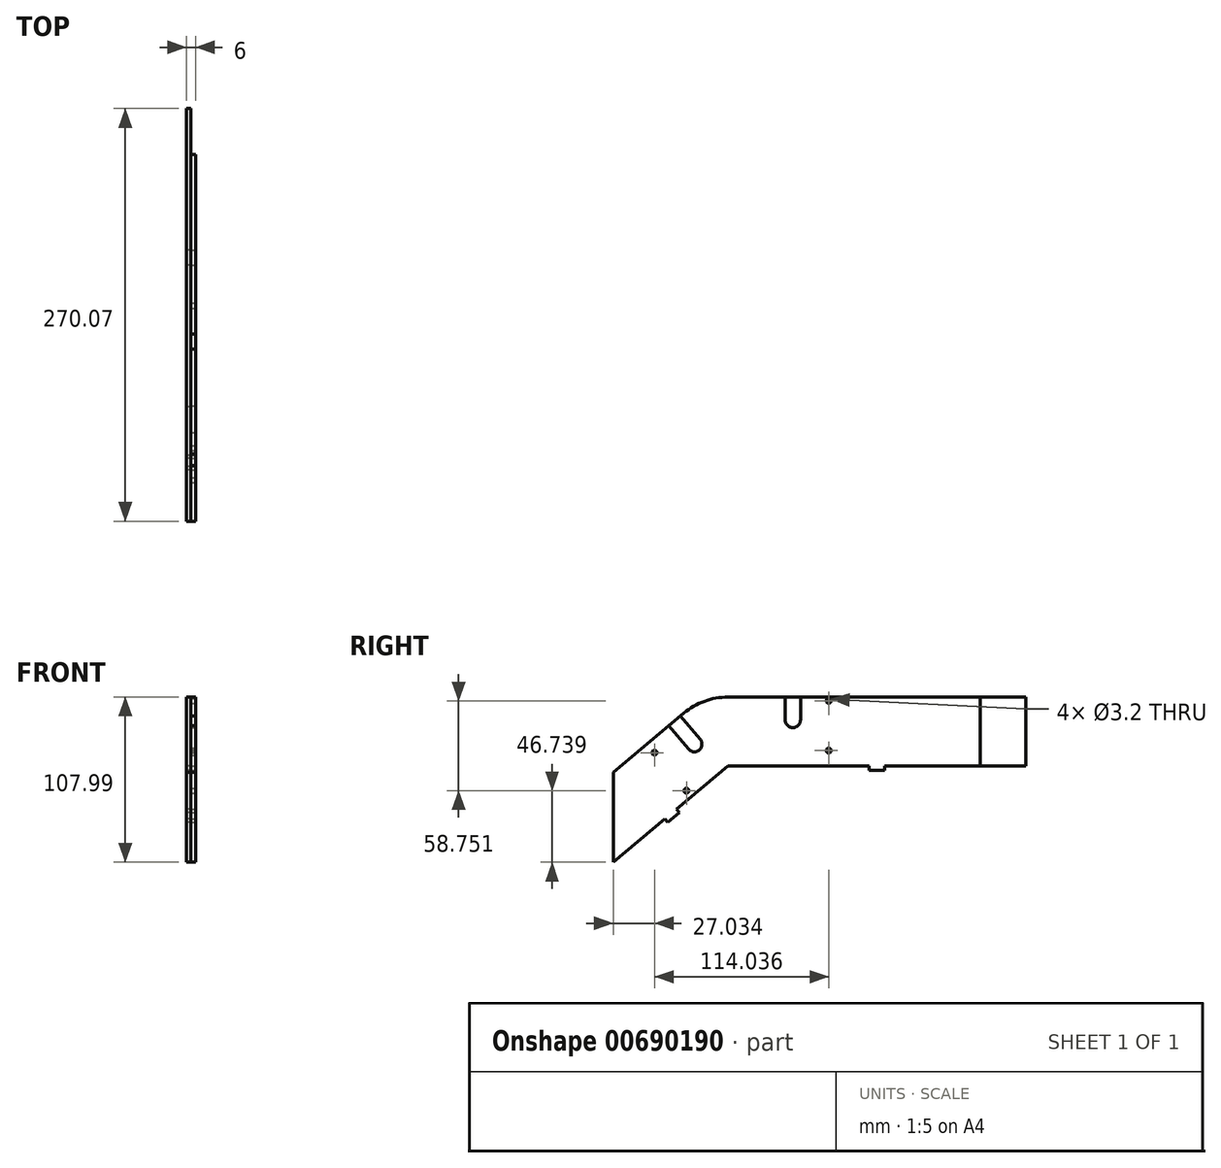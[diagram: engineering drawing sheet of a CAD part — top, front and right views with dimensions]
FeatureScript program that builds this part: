
annotation { "Feature Type Name" : "Feature", "Feature Type Description" : "" }
export const myFeature = defineFeature(function(context is Context, id is Id, definition is map)
    precondition{}
    {
        {
            var Q0;
            Q0=qCreatedBy(makeId("Right.planeOp"),FACE);
            var sketch = newSketch(context, id + "F0", { "sketchPlane" : qUnion([Q0])});
            skLineSegment(sketch, "E0.bottom", {"start": v(-97.5, 0) * mm, "end": v(97.5, 0) * mm});
            skLineSegment(sketch, "E0.top", {"start": v(-97.5, 45) * mm, "end": v(97.5, 45) * mm});
            skLineSegment(sketch, "E0.left", {"start": v(-97.5, 0) * mm, "end": v(-97.5, 45) * mm, "construction": true});
            skLineSegment(sketch, "E0.right", {"start": v(97.5, 0) * mm, "end": v(97.5, 45) * mm});
            skPoint(sketch, "E0.middle", {"position": v(0, 22.5) * mm});
            skLineSegment(sketch, "E1", {"start": v(-97.5, 0) * mm, "end": v(-172.57, -63) * mm});
            skLineSegment(sketch, "E2", {"start": v(-172.57, -63) * mm, "end": v(-201.5, -28.52) * mm});
            skLineSegment(sketch, "E3", {"start": v(-201.5, -28.52) * mm, "end": v(-126.43, 34.47) * mm});
            skLineSegment(sketch, "E4", {"start": v(-97.5, 0) * mm, "end": v(-126.43, 34.47) * mm, "construction": true});
            skArc(sketch, "E5", {"start": v(-97.5, 45) * mm, "mid": v(-112.9, 42.29) * mm, "end": v(-126.43, 34.47) * mm});
            skSolve(sketch);
        }
        {
            var Q0;
            Q0=makeQuery(id+"F0.imprint","IMPRINT",FACE,{"disambiguationData":[TD([[makeQuery(id+"F0.imprint","IMPRINT",EDGE,{"derivedFrom":sQuery(id+"F0.wireOp",EDGE,"E0.bottom")}),1.0]])]});
            extrude(context, id + "F1", {"entities" : qUnion([Q0]), "depth" : 3 * mm, "offsetDistance" : 25 * mm});
        }
        {
            var Q0;
            Q0=makeQuery(id+"F1.opExtrude","CAP_FACE",FACE,{"disambiguationData":[OSD([sQuery(id+"F0.wireOp",EDGE,"E0.bottom"),sQuery(id+"F0.wireOp",EDGE,"E0.top"),sQuery(id+"F0.wireOp",EDGE,"E0.left"),sQuery(id+"F0.wireOp",EDGE,"E0.right")])],"isStart":false});
            var sketch = newSketch(context, id + "F2", { "sketchPlane" : qUnion([Q0])});
            skLineSegment(sketch, "E6.bottom", {"start": v(4.95, 0) * mm, "end": v(-4.95, 0) * mm});
            skLineSegment(sketch, "E6.top", {"start": v(4.95, -3) * mm, "end": v(-4.95, -3) * mm});
            skLineSegment(sketch, "E6.left", {"start": v(4.95, 0) * mm, "end": v(4.95, -3) * mm});
            skLineSegment(sketch, "E6.right", {"start": v(-4.95, 0) * mm, "end": v(-4.95, -3) * mm});
            skPoint(sketch, "E6.middle", {"position": v(0, -1.5) * mm});
            skLineSegment(sketch, "E7", {"start": v(-138.83, -34.68) * mm, "end": v(-136.9, -36.98) * mm});
            skLineSegment(sketch, "E8", {"start": v(-136.9, -36.98) * mm, "end": v(-129.32, -30.61) * mm});
            skLineSegment(sketch, "E9", {"start": v(-129.32, -30.61) * mm, "end": v(-131.24, -28.31) * mm});
            skLineSegment(sketch, "E10", {"start": v(-131.24, -28.31) * mm, "end": v(-138.83, -34.68) * mm});
            skSolve(sketch);
        }
        {
            var Q0;
            Q0=makeQuery(id+"F2.imprint","IMPRINT",FACE,{"disambiguationData":[TD([[makeQuery(id+"F2.imprint","IMPRINT",EDGE,{"derivedFrom":sQuery(id+"F2.wireOp",EDGE,"E6.bottom")}),-1.0]])]});
            var Q1;
            Q1=makeQuery(id+"F2.imprint","IMPRINT",FACE,{"disambiguationData":[TD([[makeQuery(id+"F2.imprint","IMPRINT",EDGE,{"derivedFrom":sQuery(id+"F2.wireOp",EDGE,"E7")}),1.0]])]});
            var Q2;
            Q2=makeQuery(id+"F1.opExtrude","CAP_FACE",FACE,{"disambiguationData":[OSD([sQuery(id+"F0.wireOp",EDGE,"E0.bottom"),sQuery(id+"F0.wireOp",EDGE,"E0.top"),sQuery(id+"F0.wireOp",EDGE,"E0.left"),sQuery(id+"F0.wireOp",EDGE,"E0.right")])],"isStart":true});
            extrude(context, id + "F3", {"entities" : qUnion([Q0, Q1]), "operationType" : NewBodyOperationType.ADD, "endBound" : BoundingType.UP_TO_SURFACE, "oppositeDirection" : true, "depth" : 25 * mm, "endBoundEntityFace" : qUnion([Q2]), "offsetDistance" : 25 * mm});
        }
        {
            var Q0;
            Q0=makeQuery(id+"F3.boolean.opBoolean","MERGE",FACE,{"derivedFrom":[makeQuery(id+"F1.opExtrude","CAP_FACE",FACE,{"disambiguationData":[OSD([sQuery(id+"F0.wireOp",EDGE,"E0.bottom"),sQuery(id+"F0.wireOp",EDGE,"E0.top"),sQuery(id+"F0.wireOp",EDGE,"E0.right"),sQuery(id+"F0.wireOp",EDGE,"E1"),sQuery(id+"F0.wireOp",EDGE,"E2"),sQuery(id+"F0.wireOp",EDGE,"E3"),sQuery(id+"F0.wireOp",EDGE,"E5")])],"isStart":false}),makeQuery(id+"F3.opExtrude","CAP_FACE",FACE,{"disambiguationData":[OSD([sQuery(id+"F2.wireOp",EDGE,"E6.bottom"),sQuery(id+"F2.wireOp",EDGE,"E6.top"),sQuery(id+"F2.wireOp",EDGE,"E6.left"),sQuery(id+"F2.wireOp",EDGE,"E6.right")])],"isStart":true}),makeQuery(id+"F3.opExtrude","CAP_FACE",FACE,{"disambiguationData":[OSD([sQuery(id+"F2.wireOp",EDGE,"E7"),sQuery(id+"F2.wireOp",EDGE,"E8"),sQuery(id+"F2.wireOp",EDGE,"E9"),sQuery(id+"F2.wireOp",EDGE,"E10")])],"isStart":true})]});
            var sketch = newSketch(context, id + "F4", { "sketchPlane" : qUnion([Q0])});
            skLineSegment(sketch, "E11", {"start": v(-172.57, -63) * mm, "end": v(-172.57, -4.25) * mm});
            skLineSegment(sketch, "E12", {"start": v(-172.57, -4.25) * mm, "end": v(-201.5, -28.52) * mm});
            skLineSegment(sketch, "E13", {"start": v(-201.5, -28.52) * mm, "end": v(-172.57, -63) * mm});
            skSolve(sketch);
        }
        {
            var Q0;
            Q0=makeQuery(id+"F4.imprint","IMPRINT",FACE,{"disambiguationData":[TD([[makeQuery(id+"F4.imprint","IMPRINT",EDGE,{"derivedFrom":sQuery(id+"F4.wireOp",EDGE,"E11")}),1.0]])]});
            extrude(context, id + "F5", {"entities" : qUnion([Q0]), "operationType" : NewBodyOperationType.REMOVE, "endBound" : BoundingType.UP_TO_NEXT, "oppositeDirection" : true, "depth" : 25 * mm, "offsetDistance" : 25 * mm});
        }
        {
            var Q0;
            Q0=makeQuery(id+"F1.opExtrude","SWEPT_BODY",BODY,{"disambiguationData":[OSD([sQuery(id+"F0.wireOp",EDGE,"E0.bottom"),sQuery(id+"F0.wireOp",EDGE,"E0.top"),sQuery(id+"F0.wireOp",EDGE,"E0.left"),sQuery(id+"F0.wireOp",EDGE,"E0.right")])]});
            var Q1;
            Q1=qCreatedBy(makeId("Right.planeOp"),FACE);
            mirror(context, id + "F6", {"entities" : qUnion([Q0]), "mirrorPlane" : qUnion([Q1])});
        }
        {
            var Q0;
            Q0=makeQuery(id+"F3.boolean.opBoolean","MERGE",FACE,{"derivedFrom":[makeQuery(id+"F1.opExtrude","CAP_FACE",FACE,{"disambiguationData":[OSD([sQuery(id+"F0.wireOp",EDGE,"E0.bottom"),sQuery(id+"F0.wireOp",EDGE,"E0.top"),sQuery(id+"F0.wireOp",EDGE,"E0.right"),sQuery(id+"F0.wireOp",EDGE,"E1"),sQuery(id+"F0.wireOp",EDGE,"E2"),sQuery(id+"F0.wireOp",EDGE,"E3"),sQuery(id+"F0.wireOp",EDGE,"E5")])],"isStart":false}),makeQuery(id+"F3.opExtrude","CAP_FACE",FACE,{"disambiguationData":[OSD([sQuery(id+"F2.wireOp",EDGE,"E6.bottom"),sQuery(id+"F2.wireOp",EDGE,"E6.top"),sQuery(id+"F2.wireOp",EDGE,"E6.left"),sQuery(id+"F2.wireOp",EDGE,"E6.right")])],"isStart":true}),makeQuery(id+"F3.opExtrude","CAP_FACE",FACE,{"disambiguationData":[OSD([sQuery(id+"F2.wireOp",EDGE,"E7"),sQuery(id+"F2.wireOp",EDGE,"E8"),sQuery(id+"F2.wireOp",EDGE,"E9"),sQuery(id+"F2.wireOp",EDGE,"E10")])],"isStart":true})]});
            var sketch = newSketch(context, id + "F7", { "sketchPlane" : qUnion([Q0])});
            skLineSegment(sketch, "E14.bottom", {"start": v(97.5, 45) * mm, "end": v(67.5, 45) * mm});
            skLineSegment(sketch, "E14.top", {"start": v(97.5, 0) * mm, "end": v(67.5, 0) * mm});
            skLineSegment(sketch, "E14.left", {"start": v(97.5, 45) * mm, "end": v(97.5, 0) * mm});
            skLineSegment(sketch, "E14.right", {"start": v(67.5, 45) * mm, "end": v(67.5, 0) * mm});
            skSolve(sketch);
        }
        {
            var Q0;
            Q0=makeQuery(id+"F7.imprint","IMPRINT",FACE,{"disambiguationData":[TD([[makeQuery(id+"F7.imprint","IMPRINT",EDGE,{"derivedFrom":sQuery(id+"F7.wireOp",EDGE,"E14.bottom")}),-1.0]])]});
            extrude(context, id + "F8", {"entities" : qUnion([Q0]), "operationType" : NewBodyOperationType.REMOVE, "endBound" : BoundingType.UP_TO_NEXT, "oppositeDirection" : true, "depth" : 25 * mm, "offsetDistance" : 25 * mm});
        }
        {
            var Q0;
            Q0=makeQuery(id+"F3.boolean.opBoolean","MERGE",FACE,{"derivedFrom":[makeQuery(id+"F1.opExtrude","CAP_FACE",FACE,{"disambiguationData":[OSD([sQuery(id+"F0.wireOp",EDGE,"E0.bottom"),sQuery(id+"F0.wireOp",EDGE,"E0.top"),sQuery(id+"F0.wireOp",EDGE,"E0.right"),sQuery(id+"F0.wireOp",EDGE,"E1"),sQuery(id+"F0.wireOp",EDGE,"E2"),sQuery(id+"F0.wireOp",EDGE,"E3"),sQuery(id+"F0.wireOp",EDGE,"E5")])],"isStart":false}),makeQuery(id+"F3.opExtrude","CAP_FACE",FACE,{"disambiguationData":[OSD([sQuery(id+"F2.wireOp",EDGE,"E6.bottom"),sQuery(id+"F2.wireOp",EDGE,"E6.top"),sQuery(id+"F2.wireOp",EDGE,"E6.left"),sQuery(id+"F2.wireOp",EDGE,"E6.right")])],"isStart":true}),makeQuery(id+"F3.opExtrude","CAP_FACE",FACE,{"disambiguationData":[OSD([sQuery(id+"F2.wireOp",EDGE,"E7"),sQuery(id+"F2.wireOp",EDGE,"E8"),sQuery(id+"F2.wireOp",EDGE,"E9"),sQuery(id+"F2.wireOp",EDGE,"E10")])],"isStart":true})]});
            var sketch = newSketch(context, id + "F9", { "sketchPlane" : qUnion([Q0])});
            skLineSegment(sketch, "E15", {"start": v(-145.54, 8.65) * mm, "end": v(-124.65, -16.25) * mm, "construction": true});
            skSolve(sketch);
        }
        {
            var Q0;
            Q0=sQuery(id+"F9.wireOp",VERTEX,"E15.end");
            var Q1;
            Q1=sQuery(id+"F9.wireOp",VERTEX,"E15.start");
            var Q2;
            Q2=makeQuery(id+"F1.opExtrude","SWEPT_BODY",BODY,{"disambiguationData":[OSD([sQuery(id+"F0.wireOp",EDGE,"E0.bottom"),sQuery(id+"F0.wireOp",EDGE,"E0.top"),sQuery(id+"F0.wireOp",EDGE,"E0.right"),sQuery(id+"F0.wireOp",EDGE,"E1"),sQuery(id+"F0.wireOp",EDGE,"E2"),sQuery(id+"F0.wireOp",EDGE,"E3"),sQuery(id+"F0.wireOp",EDGE,"E5")])]});
            hole(context, id + "F10", {"style" : HoleStyle.SIMPLE, "endStyle" : HoleEndStyle.BLIND, "holeDiameter" : 3.2 * mm, "majorDiameter" : 5 * mm, "holeDepth" : 4 * mm, "isTappedThrough" : true, "tappedDepth" : 2.3 * mm, "tapClearance" : 3, "startFromSketch" : true, "locations" : qUnion([Q0, Q1]), "scope" : qUnion([Q2])});
        }
        {
            var Q0;
            Q0=makeQuery(id+"F3.boolean.opBoolean","MERGE",FACE,{"derivedFrom":[makeQuery(id+"F1.opExtrude","CAP_FACE",FACE,{"disambiguationData":[OSD([sQuery(id+"F0.wireOp",EDGE,"E0.bottom"),sQuery(id+"F0.wireOp",EDGE,"E0.top"),sQuery(id+"F0.wireOp",EDGE,"E0.right"),sQuery(id+"F0.wireOp",EDGE,"E1"),sQuery(id+"F0.wireOp",EDGE,"E2"),sQuery(id+"F0.wireOp",EDGE,"E3"),sQuery(id+"F0.wireOp",EDGE,"E5")])],"isStart":false}),makeQuery(id+"F3.opExtrude","CAP_FACE",FACE,{"disambiguationData":[OSD([sQuery(id+"F2.wireOp",EDGE,"E6.bottom"),sQuery(id+"F2.wireOp",EDGE,"E6.top"),sQuery(id+"F2.wireOp",EDGE,"E6.left"),sQuery(id+"F2.wireOp",EDGE,"E6.right")])],"isStart":true}),makeQuery(id+"F3.opExtrude","CAP_FACE",FACE,{"disambiguationData":[OSD([sQuery(id+"F2.wireOp",EDGE,"E7"),sQuery(id+"F2.wireOp",EDGE,"E8"),sQuery(id+"F2.wireOp",EDGE,"E9"),sQuery(id+"F2.wireOp",EDGE,"E10")])],"isStart":true})]});
            var sketch = newSketch(context, id + "F11", { "sketchPlane" : qUnion([Q0])});
            skLineSegment(sketch, "E16", {"start": v(-136.19, 26.28) * mm, "end": v(-123.33, 10.96) * mm});
            skLineSegment(sketch, "E17", {"start": v(-128.52, 32.71) * mm, "end": v(-115.67, 17.39) * mm});
            skLineSegment(sketch, "E18", {"start": v(-136.19, 26.28) * mm, "end": v(-128.52, 32.71) * mm});
            skPoint(sketch, "E19", {"position": v(-145.54, 8.65) * mm});
            skArc(sketch, "E20", {"start": v(-123.33, 10.96) * mm, "mid": v(-116.29, 10.35) * mm, "end": v(-115.67, 17.39) * mm});
            skSolve(sketch);
        }
        {
            var Q0;
            Q0=makeQuery(id+"F11.imprint","IMPRINT",FACE,{"disambiguationData":[TD([[makeQuery(id+"F11.imprint","IMPRINT",EDGE,{"derivedFrom":sQuery(id+"F11.wireOp",EDGE,"E16")}),1.0]])]});
            extrude(context, id + "F12", {"entities" : qUnion([Q0]), "operationType" : NewBodyOperationType.REMOVE, "endBound" : BoundingType.UP_TO_NEXT, "oppositeDirection" : true, "depth" : 25 * mm, "offsetDistance" : 25 * mm});
        }
        {
            var Q0;
            Q0=makeQuery(id+"F3.boolean.opBoolean","MERGE",FACE,{"derivedFrom":[makeQuery(id+"F1.opExtrude","CAP_FACE",FACE,{"disambiguationData":[OSD([sQuery(id+"F0.wireOp",EDGE,"E0.bottom"),sQuery(id+"F0.wireOp",EDGE,"E0.top"),sQuery(id+"F0.wireOp",EDGE,"E0.right"),sQuery(id+"F0.wireOp",EDGE,"E1"),sQuery(id+"F0.wireOp",EDGE,"E2"),sQuery(id+"F0.wireOp",EDGE,"E3"),sQuery(id+"F0.wireOp",EDGE,"E5")])],"isStart":false}),makeQuery(id+"F3.opExtrude","CAP_FACE",FACE,{"disambiguationData":[OSD([sQuery(id+"F2.wireOp",EDGE,"E6.bottom"),sQuery(id+"F2.wireOp",EDGE,"E6.top"),sQuery(id+"F2.wireOp",EDGE,"E6.left"),sQuery(id+"F2.wireOp",EDGE,"E6.right")])],"isStart":true}),makeQuery(id+"F3.opExtrude","CAP_FACE",FACE,{"disambiguationData":[OSD([sQuery(id+"F2.wireOp",EDGE,"E7"),sQuery(id+"F2.wireOp",EDGE,"E8"),sQuery(id+"F2.wireOp",EDGE,"E9"),sQuery(id+"F2.wireOp",EDGE,"E10")])],"isStart":true})]});
            var sketch = newSketch(context, id + "F13", { "sketchPlane" : qUnion([Q0])});
            skLineSegment(sketch, "E21", {"start": v(-31.5, 42.5) * mm, "end": v(-31.5, 10) * mm, "construction": true});
            skLineSegment(sketch, "E22", {"start": v(-60, 45) * mm, "end": v(-60, 30) * mm});
            skLineSegment(sketch, "E23", {"start": v(-60, 45) * mm, "end": v(-50, 45) * mm});
            skLineSegment(sketch, "E24", {"start": v(-50, 45) * mm, "end": v(-50, 30) * mm});
            skArc(sketch, "E25", {"start": v(-60, 30) * mm, "mid": v(-55, 25) * mm, "end": v(-50, 30) * mm});
            skSolve(sketch);
        }
        {
            var Q0;
            Q0=sQuery(id+"F13.wireOp",VERTEX,"E21.start");
            var Q1;
            Q1=sQuery(id+"F13.wireOp",VERTEX,"E21.end");
            var Q2;
            Q2=makeQuery(id+"F1.opExtrude","SWEPT_BODY",BODY,{"disambiguationData":[OSD([sQuery(id+"F0.wireOp",EDGE,"E0.bottom"),sQuery(id+"F0.wireOp",EDGE,"E0.top"),sQuery(id+"F0.wireOp",EDGE,"E0.right"),sQuery(id+"F0.wireOp",EDGE,"E1"),sQuery(id+"F0.wireOp",EDGE,"E2"),sQuery(id+"F0.wireOp",EDGE,"E3"),sQuery(id+"F0.wireOp",EDGE,"E5")])]});
            hole(context, id + "F14", {"style" : HoleStyle.SIMPLE, "endStyle" : HoleEndStyle.BLIND, "holeDiameter" : 3.2 * mm, "majorDiameter" : 5 * mm, "holeDepth" : 4 * mm, "isTappedThrough" : true, "tappedDepth" : 2.3 * mm, "tapClearance" : 3, "startFromSketch" : true, "locations" : qUnion([Q0, Q1]), "scope" : qUnion([Q2])});
        }
        {
            var Q0;
            Q0=makeQuery(id+"F13.imprint","IMPRINT",FACE,{"disambiguationData":[TD([[makeQuery(id+"F13.imprint","IMPRINT",EDGE,{"derivedFrom":sQuery(id+"F13.wireOp",EDGE,"E22")}),1.0]])]});
            extrude(context, id + "F15", {"entities" : qUnion([Q0]), "operationType" : NewBodyOperationType.REMOVE, "endBound" : BoundingType.UP_TO_NEXT, "oppositeDirection" : true, "depth" : 25 * mm, "offsetDistance" : 25 * mm});
        }
    });
